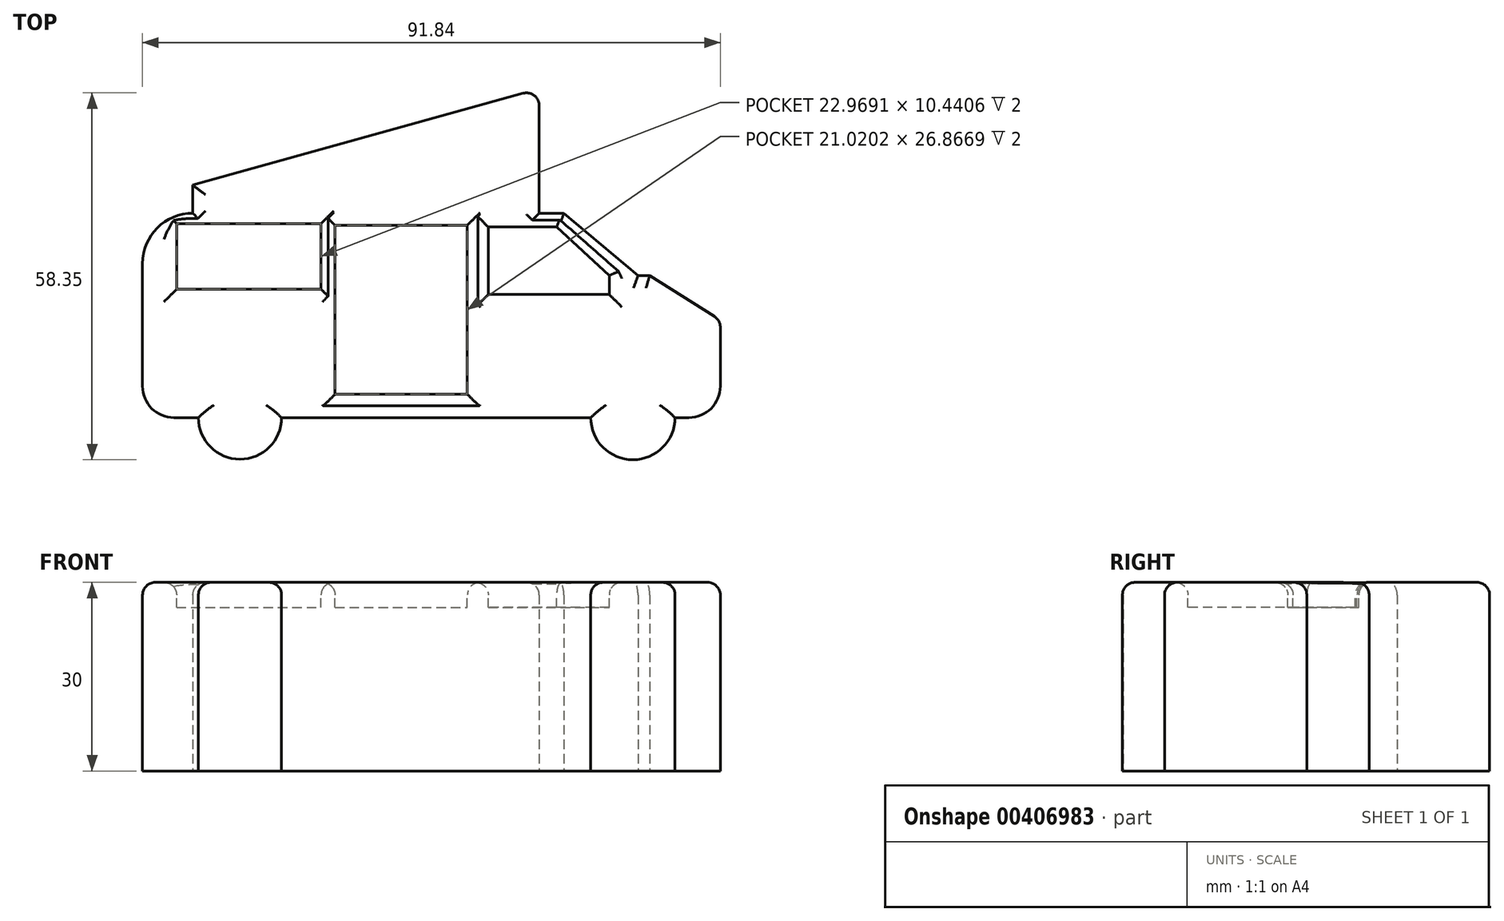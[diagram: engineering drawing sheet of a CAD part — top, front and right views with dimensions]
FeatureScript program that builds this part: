
annotation { "Feature Type Name" : "Feature", "Feature Type Description" : "" }
export const myFeature = defineFeature(function(context is Context, id is Id, definition is map)
    precondition{}
    {
        {
            var Q0;
            Q0=qCreatedBy(makeId("Top.planeOp"),FACE);
            var sketch = newSketch(context, id + "F0", { "sketchPlane" : qUnion([Q0])});
            skArc(sketch, "E0", {"start": v(-26.6, -32.5) * mm, "mid": v(-20, -39.12) * mm, "end": v(-13.39, -32.5) * mm});
            skArc(sketch, "E1", {"start": v(35.76, -32.5) * mm, "mid": v(42.46, -39.2) * mm, "end": v(49.16, -32.5) * mm});
            skLineSegment(sketch, "E2.bottom", {"start": v(-30.49, -32.5) * mm, "end": v(51.35, -32.5) * mm});
            skLineSegment(sketch, "E2.top", {"start": v(-35.49, -21.6) * mm, "end": v(56.35, -21.6) * mm, "construction": true});
            skLineSegment(sketch, "E2.left", {"start": v(-35.49, -27.5) * mm, "end": v(-35.49, -21.6) * mm});
            skLineSegment(sketch, "E2.right", {"start": v(56.35, -27.5) * mm, "end": v(56.35, -21.6) * mm});
            skLineSegment(sketch, "E3.bottom", {"start": v(-35.49, -21.6) * mm, "end": v(27.57, -21.6) * mm, "construction": true});
            skLineSegment(sketch, "E3.top", {"start": v(-27.49, 0) * mm, "end": v(27.57, 0) * mm, "construction": true});
            skLineSegment(sketch, "E3.left", {"start": v(-35.49, -21.6) * mm, "end": v(-35.49, -8) * mm});
            skLineSegment(sketch, "E3.right", {"start": v(27.57, -21.6) * mm, "end": v(27.57, 0) * mm, "construction": true});
            skPoint(sketch, "E4.visualSharp", {"position": v(-35.49, 0) * mm});
            skArc(sketch, "E4.filletArc", {"start": v(-27.49, 0) * mm, "mid": v(-33.14, -2.34) * mm, "end": v(-35.49, -8) * mm});
            skLineSegment(sketch, "E5", {"start": v(-27.49, 0) * mm, "end": v(-27.49, 4.47) * mm});
            skLineSegment(sketch, "E6", {"start": v(-27.49, 4.47) * mm, "end": v(27.57, 19.78) * mm});
            skLineSegment(sketch, "E7", {"start": v(27.57, 19.78) * mm, "end": v(27.57, 0) * mm});
            skLineSegment(sketch, "E8", {"start": v(27.57, 0) * mm, "end": v(31.5, 0) * mm});
            skLineSegment(sketch, "E9", {"start": v(56.35, -18.12) * mm, "end": v(56.35, -21.6) * mm});
            skLineSegment(sketch, "E10", {"start": v(31.5, 0) * mm, "end": v(43.27, -9.9) * mm});
            skLineSegment(sketch, "E11", {"start": v(43.27, -9.9) * mm, "end": v(45.13, -9.9) * mm});
            skLineSegment(sketch, "E12", {"start": v(45.13, -9.9) * mm, "end": v(55.43, -16.43) * mm});
            skPoint(sketch, "E13.visualSharp", {"position": v(-35.49, -32.5) * mm});
            skArc(sketch, "E13.filletArc", {"start": v(-35.49, -27.5) * mm, "mid": v(-34.02, -31.04) * mm, "end": v(-30.49, -32.5) * mm});
            skPoint(sketch, "E14.visualSharp", {"position": v(56.35, -32.5) * mm});
            skArc(sketch, "E14.filletArc", {"start": v(51.35, -32.5) * mm, "mid": v(54.9, -31.04) * mm, "end": v(56.35, -27.5) * mm});
            skPoint(sketch, "E15.visualSharp", {"position": v(56.35, -17.02) * mm});
            skArc(sketch, "E15.filletArc", {"start": v(56.35, -18.12) * mm, "mid": v(56.1, -17.16) * mm, "end": v(55.43, -16.43) * mm});
            skSolve(sketch);
        }
        {
            var Q0;
            Q0 = qSketchRegion(id + "F0", true);
            extrude(context, id + "F1", {"entities" : qUnion([Q0]), "depth" : 30 * mm});
        }
        {
            var Q0;
            Q0=makeQuery(id+"F1.opExtrude","CAP_FACE",FACE,{"disambiguationData":[OSD([sQuery(id+"F0.wireOp",EDGE,"E0"),sQuery(id+"F0.wireOp",EDGE,"E1"),sQuery(id+"F0.wireOp",EDGE,"E2.bottom"),sQuery(id+"F0.wireOp",EDGE,"E2.left"),sQuery(id+"F0.wireOp",EDGE,"E2.right"),sQuery(id+"F0.wireOp",EDGE,"E3.left"),sQuery(id+"F0.wireOp",EDGE,"E4.filletArc"),sQuery(id+"F0.wireOp",EDGE,"E5"),sQuery(id+"F0.wireOp",EDGE,"E6"),sQuery(id+"F0.wireOp",EDGE,"E7"),sQuery(id+"F0.wireOp",EDGE,"E8"),sQuery(id+"F0.wireOp",EDGE,"E9"),sQuery(id+"F0.wireOp",EDGE,"E10"),sQuery(id+"F0.wireOp",EDGE,"E11"),sQuery(id+"F0.wireOp",EDGE,"E12"),sQuery(id+"F0.wireOp",EDGE,"E13.filletArc"),sQuery(id+"F0.wireOp",EDGE,"E14.filletArc"),sQuery(id+"F0.wireOp",EDGE,"E15.filletArc")])],"isStart":false});
            var sketch = newSketch(context, id + "F2", { "sketchPlane" : qUnion([Q0])});
            skLineSegment(sketch, "E16.bottom", {"start": v(-30.07, -12.08) * mm, "end": v(-7.1, -12.08) * mm});
            skLineSegment(sketch, "E16.top", {"start": v(-30.07, -1.64) * mm, "end": v(-7.1, -1.64) * mm});
            skLineSegment(sketch, "E16.left", {"start": v(-30.07, -12.08) * mm, "end": v(-30.07, -1.64) * mm});
            skLineSegment(sketch, "E16.right", {"start": v(-7.1, -12.08) * mm, "end": v(-7.1, -1.64) * mm});
            skLineSegment(sketch, "E17.bottom", {"start": v(-4.88, -1.92) * mm, "end": v(16.14, -1.92) * mm});
            skLineSegment(sketch, "E17.top", {"start": v(-4.88, -28.79) * mm, "end": v(16.14, -28.79) * mm});
            skLineSegment(sketch, "E17.left", {"start": v(-4.88, -1.92) * mm, "end": v(-4.88, -28.79) * mm});
            skLineSegment(sketch, "E17.right", {"start": v(16.14, -1.92) * mm, "end": v(16.14, -28.79) * mm});
            skLineSegment(sketch, "E18", {"start": v(19.47, -2.2) * mm, "end": v(19.47, -12.92) * mm});
            skLineSegment(sketch, "E19", {"start": v(19.47, -12.92) * mm, "end": v(38.7, -12.92) * mm});
            skLineSegment(sketch, "E20", {"start": v(38.7, -12.92) * mm, "end": v(38.7, -9.9) * mm});
            skLineSegment(sketch, "E21", {"start": v(38.7, -9.9) * mm, "end": v(30.34, -2.2) * mm});
            skLineSegment(sketch, "E22", {"start": v(30.34, -2.2) * mm, "end": v(19.47, -2.2) * mm});
            skLineSegment(sketch, "E23", {"start": v(-18.6, -1.64) * mm, "end": v(-19.91, -1.64) * mm});
            skLineSegment(sketch, "E24", {"start": v(-19.91, -1.64) * mm, "end": v(-19.91, -12.08) * mm, "construction": true});
            skLineSegment(sketch, "E25", {"start": v(-19.91, -12.08) * mm, "end": v(-18.6, -12.08) * mm});
            skLineSegment(sketch, "E26", {"start": v(-18.6, -12.08) * mm, "end": v(-18.6, -1.64) * mm, "construction": true});
            skSolve(sketch);
        }
        {
            var Q0;
            Q0=makeQuery(id+"F2.imprint","IMPRINT",FACE,{"disambiguationData":[TD([[makeQuery(id+"F2.imprint","IMPRINT",EDGE,{"derivedFrom":sQuery(id+"F2.wireOp",EDGE,"E18")}),1.0]])]});
            var Q1;
            Q1=makeQuery(id+"F2.imprint","IMPRINT",FACE,{"disambiguationData":[TD([[makeQuery(id+"F2.imprint","IMPRINT",EDGE,{"derivedFrom":sQuery(id+"F2.wireOp",EDGE,"E17.bottom")}),-1.0]])]});
            var Q2;
            {var subQ3=sQuery(id+"F2.wireOp",EDGE,"E16.left");Q2=makeQuery(id+"F2.imprint","IMPRINT",FACE,{"disambiguationData":[TD([[makeQuery(id+"F2.imprint","IMPRINT",EDGE,{"derivedFrom":subQ3}),-1.0]])]});}
            extrude(context, id + "F3", {"entities" : qUnion([Q0, Q1, Q2]), "operationType" : NewBodyOperationType.REMOVE, "oppositeDirection" : true, "depth" : 4 * mm});
        }
        {
            var Q0;
            Q0=makeQuery(id+"F1.opExtrude","CAP_FACE",FACE,{"disambiguationData":[OSD([sQuery(id+"F0.wireOp",EDGE,"E0"),sQuery(id+"F0.wireOp",EDGE,"E1"),sQuery(id+"F0.wireOp",EDGE,"E2.bottom"),sQuery(id+"F0.wireOp",EDGE,"E2.left"),sQuery(id+"F0.wireOp",EDGE,"E2.right"),sQuery(id+"F0.wireOp",EDGE,"E3.left"),sQuery(id+"F0.wireOp",EDGE,"E4.filletArc"),sQuery(id+"F0.wireOp",EDGE,"E5"),sQuery(id+"F0.wireOp",EDGE,"E6"),sQuery(id+"F0.wireOp",EDGE,"E7"),sQuery(id+"F0.wireOp",EDGE,"E8"),sQuery(id+"F0.wireOp",EDGE,"E9"),sQuery(id+"F0.wireOp",EDGE,"E10"),sQuery(id+"F0.wireOp",EDGE,"E11"),sQuery(id+"F0.wireOp",EDGE,"E12"),sQuery(id+"F0.wireOp",EDGE,"E13.filletArc"),sQuery(id+"F0.wireOp",EDGE,"E14.filletArc"),sQuery(id+"F0.wireOp",EDGE,"E15.filletArc")])],"isStart":false});
            fillet(context, id + "F4", {"entities" : qUnion([Q0]), "radius" : 2 * mm, "tangentPropagation" : true, "allowEdgeOverflow" : false});
        }
        {
            var Q0;
            Q0=makeQuery(id+"F1.opExtrude","SWEPT_EDGE",EDGE,{"disambiguationData":[OSD([sQuery(id+"F0.wireOp",EDGE,"E6"),sQuery(id+"F0.wireOp",EDGE,"E7")])]});
            fillet(context, id + "F5", {"entities" : qUnion([Q0]), "radius" : 2 * mm, "tangentPropagation" : true, "allowEdgeOverflow" : false});
        }
    });
